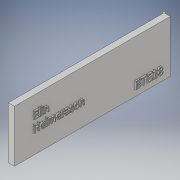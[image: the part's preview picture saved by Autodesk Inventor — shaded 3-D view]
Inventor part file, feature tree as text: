
AUTODESK INVENTOR PART (.ipt)
format: ipt  version: 2018 (Build 220112000, 112)  size: 507,392 bytes
history: native  units: mm
features: sketch x5, extrude x4
ambient origin geometry x8: Origin, YZ Plane, XZ Plane, XY Plane, X Axis, Y Axis, Z Axis, Center Point
bodies: Solid1 (feature_tree)
feature tree (9):
  extrude  "Extrusion1"  Depth=25.0mm
  extrude  "Extrusion2"  Depth=0.75mm TaperAngle=0.0deg
  sketch  "Sketch3"  dims[d6=0.75mm d7=0.0mm d8=10.0mm]
  extrude  "Extrusion3"  Depth=10.0mm
  extrude  "Extrusion4"  [1 undecoded]
  sketch  "Sketch1"  dims[d0=75.0mm d1=25.0mm]
  sketch  "Sketch2"  dims[d2=3.0mm d3=0.0mm d4=0.75mm d5=0.0mm]
  sketch  "Sketch4"  dims[d9=1.5mm d10=0.0mm]
  sketch  "Sketch5"
note: 1 required parameter value undecoded (feature->parameter linkage not recoverable at this tier; creation-order binding heuristic only, values carry confidence <= 0.55)
